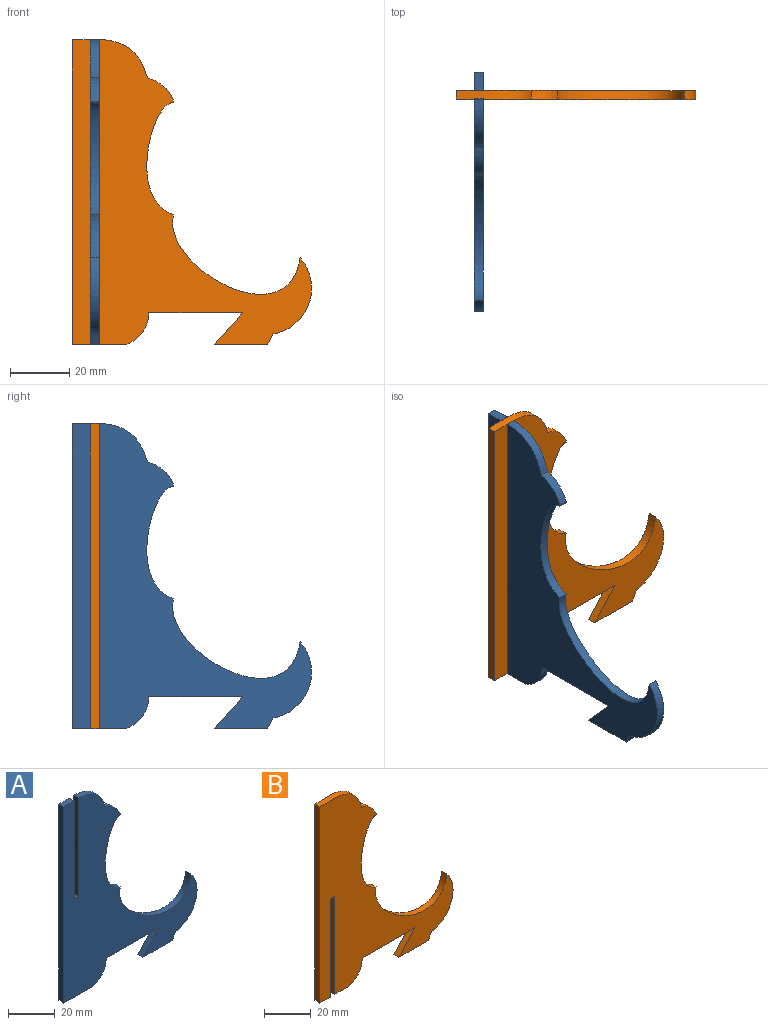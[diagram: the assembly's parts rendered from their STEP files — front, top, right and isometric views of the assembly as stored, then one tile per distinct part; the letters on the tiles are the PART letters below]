
ASSEMBLY  parts=2 mates=1
PART A: 19 faces, bbox 80.8x3x103.2 mm
  f0: plane 18x3mm, normal (0,0,-1), area 54mm2, adj f1,f16,f17,f18
  f1: cylinder r=11.36mm len=10.7mm, axis (0,1,0), area 42.4mm2, adj f0,f2,f17,f18
  f2: plane 31.7x3mm, normal (0,0,-1), area 95.1mm2, adj f1,f3,f17,f18
  f3: plane 10.7x9.57mm, normal (-0.75,0,0.67), area 43.1mm2, adj f2,f4,f17,f18
  f4: plane 18x3mm, normal (0,0,-1), area 54mm2, adj f3,f5,f17,f18
  f5: plane 3.56x3mm, normal (0.89,0,-0.46), area 12mm2, adj f4,f6,f17,f18
  f6: cylinder r=15.7mm len=25.8mm, axis (0,1,0), area 99.9mm2, adj f5,f7,f17,f18
  f7: extruded ~43.08x26.86mm, area 192.5mm2, adj f6,f8,f17,f18
  f8: extruded ~37.87x9.06mm, area 134.4mm2, adj f7,f9,f17,f18
  f9: plane 3x0.6mm, normal (1,0,0), area 1.8mm2, adj f8,f10,f17,f18
  f10: extruded ~8.88x7.83mm, area 37mm2, adj f9,f11,f17,f18
  f11: extruded ~16.32x13mm, area 68.3mm2, adj f10,f12,f17,f18
  f12: plane 51.67x3mm, normal (-1,0,0), area 155mm2, adj f11,f13,f17,f18
  f13: plane 3x2.8mm, normal (0,0,1), area 8.4mm2, adj f12,f14,f17,f18
  f14: plane 51.67x3mm, normal (1,0,0), area 155mm2, adj f13,f15,f17,f18
  f15: extruded ~6.2x3mm, area 18.6mm2, adj f14,f16,f17,f18
  f16: plane 103x3mm, normal (-1,0,0), area 309mm2, adj f0,f15,f17,f18
  f17: plane 103.17x80.85mm, normal (0,-1,0), area 3569.5mm2, adj f0,f1,f2,f3,f4,f5,f6,f7
  f18: plane 103.17x80.85mm, normal (0,1,0), area 3569.5mm2, adj f0,f1,f2,f3,f4,f5,f6,f7
PART B: 19 faces, bbox 80.8x3x105.4 mm
  f0: plane 103x3mm, normal (-1,0,0), area 309mm2, adj f1,f16,f17,f18
  f1: plane 6.2x3mm, normal (0,0,-1), area 18.6mm2, adj f0,f2,f17,f18
  f2: plane 51.5x3mm, normal (1,0,0), area 154.5mm2, adj f1,f3,f17,f18
  f3: plane 3x2.8mm, normal (0,0,-1), area 8.4mm2, adj f2,f4,f17,f18
  f4: plane 51.5x3mm, normal (-1,0,0), area 154.5mm2, adj f3,f5,f17,f18
  f5: plane 9x3mm, normal (0,0,-1), area 27mm2, adj f4,f6,f17,f18
  f6: cylinder r=11.36mm len=10.7mm, axis (0,1,0), area 42.4mm2, adj f5,f7,f17,f18
  f7: plane 31.7x3mm, normal (0,0,-1), area 95.1mm2, adj f6,f8,f17,f18
  f8: plane 10.7x9.57mm, normal (-0.75,0,0.67), area 43.1mm2, adj f7,f9,f17,f18
  f9: plane 18x3mm, normal (0,0,-1), area 54mm2, adj f8,f10,f17,f18
  f10: plane 3.56x3mm, normal (0.89,0,-0.46), area 12mm2, adj f9,f11,f17,f18
  f11: cylinder r=15.7mm len=25.8mm, axis (0,1,0), area 99.9mm2, adj f10,f12,f17,f18
  f12: extruded ~43.08x26.86mm, area 192.5mm2, adj f11,f13,f17,f18
  f13: extruded ~37.87x9.06mm, area 134.4mm2, adj f12,f14,f17,f18
  f14: plane 3x0.6mm, normal (1,0,0), area 1.8mm2, adj f13,f15,f17,f18
  f15: extruded ~8.88x7.83mm, area 37mm2, adj f14,f16,f17,f18
  f16: extruded ~25.32x13.02mm, area 95.3mm2, adj f0,f15,f17,f18
  f17: plane 105.38x80.85mm, normal (0,-1,0), area 3570mm2, adj f0,f1,f2,f3,f4,f5,f6,f7
  f18: plane 105.38x80.85mm, normal (0,1,0), area 3570mm2, adj f0,f1,f2,f3,f4,f5,f6,f7
PLACE A rot(axis=(0,0,-1),90deg) t=(-33.74,30.65,-15.21)mm
PLACE B t=(-42.84,24.55,-15.21)mm
MATE slider A.f13 <-> B.f3  axis (0,0,1) through (-35.24,23.05,36.29)mm
